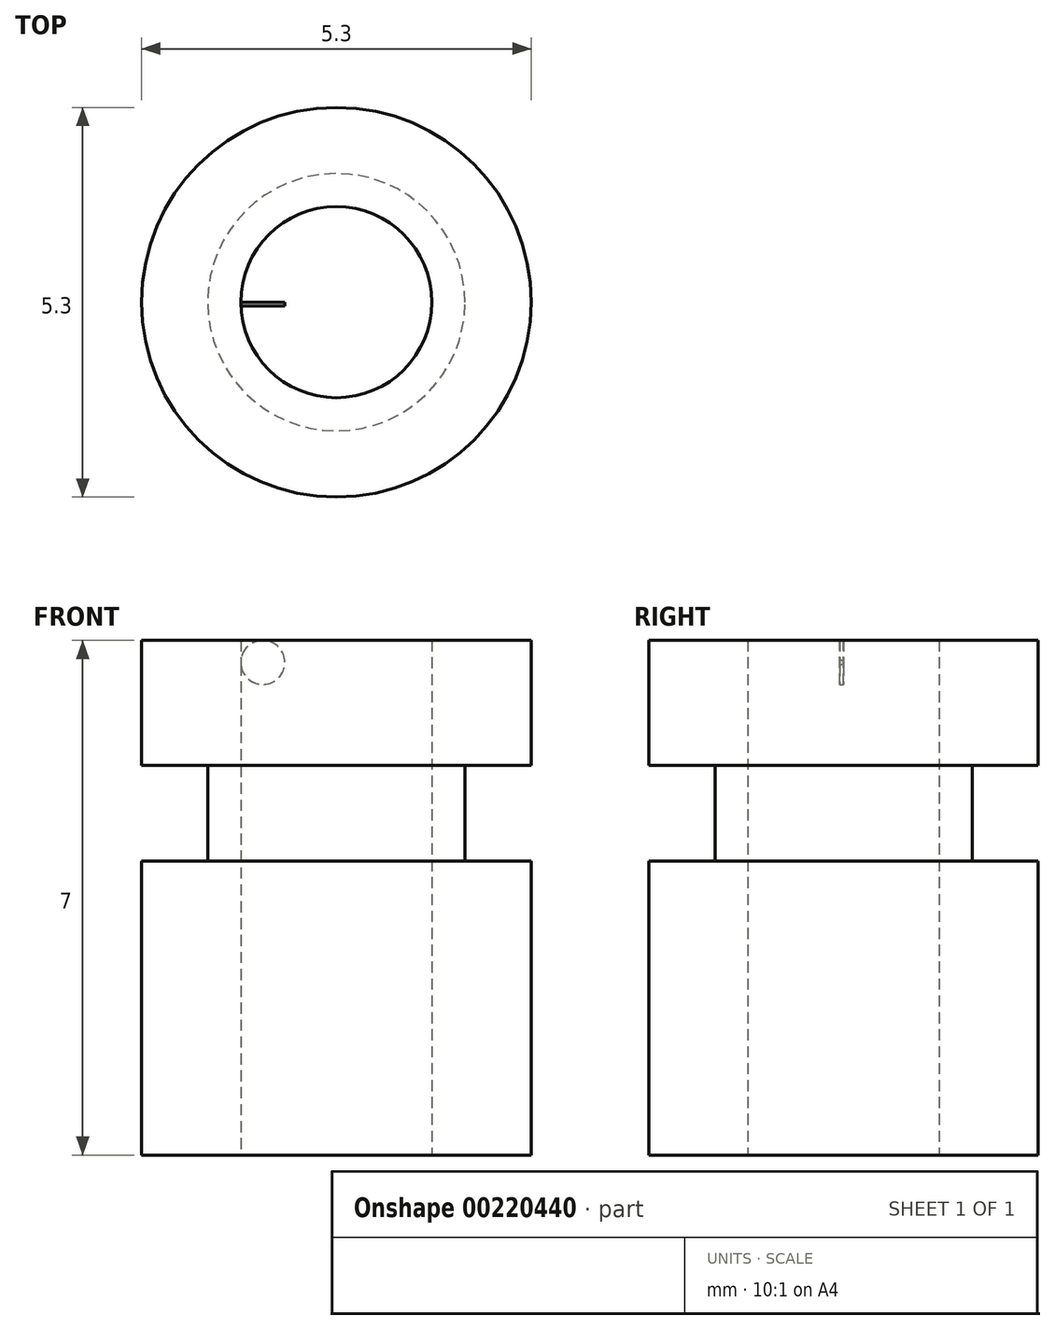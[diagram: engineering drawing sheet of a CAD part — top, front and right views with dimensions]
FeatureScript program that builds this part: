
annotation { "Feature Type Name" : "Feature", "Feature Type Description" : "" }
export const myFeature = defineFeature(function(context is Context, id is Id, definition is map)
    precondition{}
    {
        {
            var Q0;
            Q0=qCreatedBy(makeId("Front.planeOp"),FACE);
            var sketch = newSketch(context, id + "F0", { "sketchPlane" : qUnion([Q0])});
            skLineSegment(sketch, "E0", {"start": v(1.3, 7) * mm, "end": v(2.65, 7) * mm});
            skLineSegment(sketch, "E1", {"start": v(1.3, 0) * mm, "end": v(2.65, 0) * mm});
            skLineSegment(sketch, "E2", {"start": v(1.3, 7) * mm, "end": v(1.3, 0) * mm});
            skLineSegment(sketch, "E3", {"start": v(2.65, 0) * mm, "end": v(2.65, 4) * mm});
            skLineSegment(sketch, "E4", {"start": v(2.65, 4) * mm, "end": v(1.75, 4) * mm});
            skLineSegment(sketch, "E5", {"start": v(1.75, 4) * mm, "end": v(1.75, 5.3) * mm});
            skLineSegment(sketch, "E6", {"start": v(1.75, 5.3) * mm, "end": v(2.65, 5.3) * mm});
            skLineSegment(sketch, "E7", {"start": v(2.65, 5.3) * mm, "end": v(2.65, 7) * mm});
            skLineSegment(sketch, "E8", {"start": v(0, 0) * mm, "end": v(0, 7.31) * mm});
            skSolve(sketch);
        }
        {
            var Q0;
            Q0=makeQuery(id+"F0.imprint","IMPRINT",FACE,{"disambiguationData":[TD([[makeQuery(id+"F0.imprint","IMPRINT",EDGE,{"derivedFrom":sQuery(id+"F0.wireOp",EDGE,"E0")}),-1.0]])]});
            var Q1;
            Q1=sQuery(id+"F0.wireOp",EDGE,"E8");
            revolve(context, id + "F1", {"entities" : qUnion([Q0]), "axis" : qUnion([Q1]), "revolveType" : RevolveType.FULL});
        }
        {
            var Q0;
            Q0=qCreatedBy(makeId("Front.planeOp"),FACE);
            var sketch = newSketch(context, id + "F2", { "sketchPlane" : qUnion([Q0])});
            skLineSegment(sketch, "E9", {"start": v(-1, 7) * mm, "end": v(-1, 6.7) * mm});
            skCircle(sketch, "E10", {"center": v(-1, 6.7) * mm, "radius": 0.3 * mm});
            skSolve(sketch);
        }
        {
            var Q0;
            Q0 = qSketchRegion(id + "F2", true);
            extrude(context, id + "F3", {"entities" : qUnion([Q0]), "operationType" : NewBodyOperationType.ADD, "depth" : 0.05 * mm});
        }
    });
